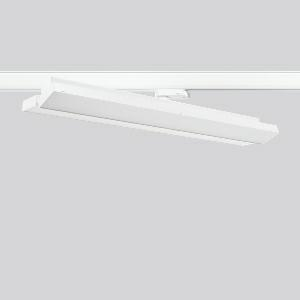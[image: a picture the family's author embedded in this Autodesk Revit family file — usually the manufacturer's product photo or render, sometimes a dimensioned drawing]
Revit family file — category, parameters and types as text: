
# Revit family: tx-move_742164_002_3_76_453b
name_source: partatom
category: Lighting Fixtures
units: mm (PartAtom-declared; Revit-internal decimal feet)

## family parameters
Cut with Voids When Loaded = No
Host = Face
Light Source = No
Part Type = Normal
Room Calculation Point = No
Round Connector Dimension = Use Diameter
Shared = No

## types (1)
- MultiLumen 1 (1 x LED Modul 835, 2550 lm, 3500)
    Apparent Load = 41 VA
    CIE Flux Codes = 47 79 96 100 100
    Color Rendering = 80
    Color Temperature = 3500
    Default Elevation = 1800 mm
    Description = Series: TX-MOVE
Multifunctional surface-mounted spotlight for area lighting. Very flat design. Housing: sheet steel, powder-coated. Rotation range: 356°. Swivel range: 90°. Consistent alignment possible with visible tilt scale. High-efficiency LED units with flush-mounted opal diffuser made of non-yellowing PMMA. Symmetrical wide beam light emission. With adapter for RZB 3-circuit DALI tracks. Suitable for Track on ceiling. MultiLumen: Luminous flux adjustable in 3 steps. Factory setting is the highest luminous flux. Environmentally friendly and resource-saving due to replaceable and recyclable components. 
Colour: traffic white, matt (RAL 9016)
Length: 570 mm
Width: 119 mm
Height: 88 mm
Lamp: LED
Socket: without socket
Colour temperature: 3500K
Colour rendering index (CRI): 80
System power: 41 W
Rated luminous flux: 5100 lm
Luminous efficiency: 124 lm/W
System power 2: 57 W
Rated luminous flux 2: 6950 lm
Luminous efficiency 2: 122 lm/W
System power 3: 73 W
Rated luminous flux 3: 8500 lm
Luminous efficiency 3: 116 lm/W
Control gear: Dimmable EVG, DALI
Protection class: I
Type of protection: IP 20
    Height = 75 mm
    Lamp = 1 x LED Modul 835
    Lamp Light Flux = 2550 lm
    Lamp count = 1
    Length = 569 mm
    Lifetime = 50000 h
    Luminous efficacy = 124 lm/W
    Manufacturer = RZB
    ModVariant = No
    Model = 742164.002.3.76
    Mounting Place = Ceiling
    Mounting Type = Rail mounted
    Number of Poles = 1
    OnlyDefault = Yes
    Power Factor = 1
    Product Name = TX-MOVE
    Product group = Track mounted projectors
    ProductGroupID = 301
    Protection Class = Protection class I
    Protection Degree = IP 20
    RLX_Detail_Level = 1
    RLX_Emergency_Light_Flux = 0 lm
    RLX_Emergency_Type = 0
    RLX_Emergency_Type_DB = No
    RlxData = <blob elided: 29869 chars, md5=ff287bba>
    Socket = socket
    Standby Power = 0 W
    System Light Flux = 5100 lm
    System Power = 41 W
    Type Comments = MultiLumen 1
    Type Image = 742164.002.jpg
    URL = http://relux.com
    VarID = multilumen_1
    Voltage = 230 V
    Voltage Range = 220-240 V
    Weight = 0.00 kg
    Width = 119 mm

## geometry (parser evidence)
native form markers: Blend x4, Sweep x12
no freeform markers — native parametric forms only
